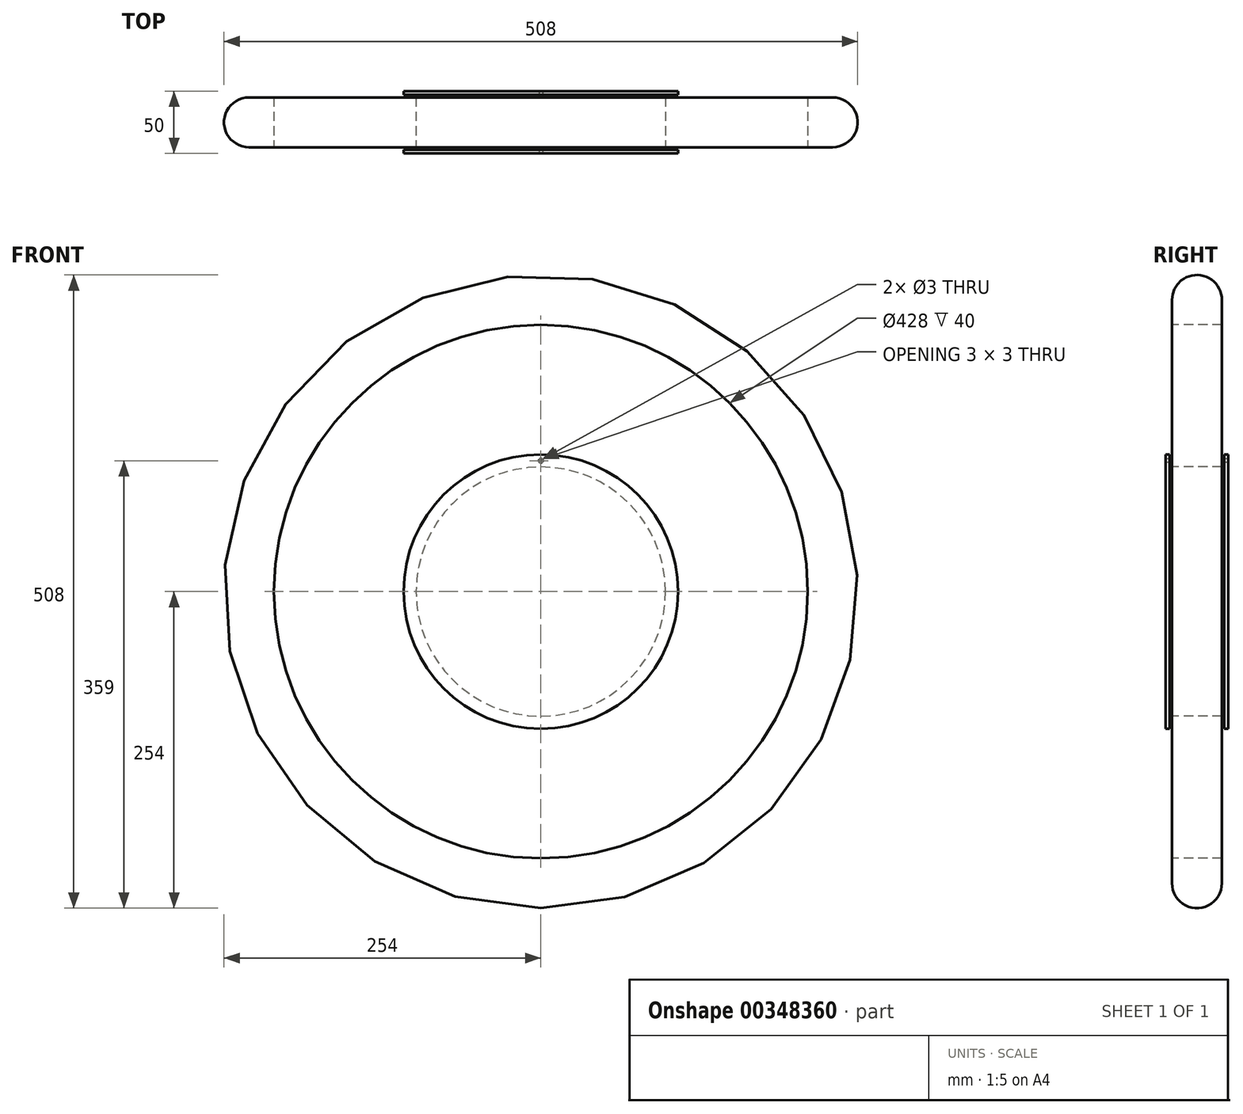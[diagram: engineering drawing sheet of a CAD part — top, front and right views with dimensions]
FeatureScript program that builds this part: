
annotation { "Feature Type Name" : "Feature", "Feature Type Description" : "" }
export const myFeature = defineFeature(function(context is Context, id is Id, definition is map)
    precondition{}
    {
        {
            var Q0;
            Q0=qCreatedBy(makeId("Top.planeOp"),FACE);
            var sketch = newSketch(context, id + "F0", { "sketchPlane" : qUnion([Q0])});
            skLineSegment(sketch, "E0", {"start": v(0, 0) * mm, "end": v(0, 101.57) * mm});
            skSolve(sketch);
        }
        {
            var Q0;
            Q0=qCreatedBy(makeId("Right.planeOp"),FACE);
            var sketch = newSketch(context, id + "F1", { "sketchPlane" : qUnion([Q0])});
            skLineSegment(sketch, "E1", {"start": v(0, 0) * mm, "end": v(0, 100) * mm, "construction": true});
            skLineSegment(sketch, "E2.bottom", {"start": v(25, 100) * mm, "end": v(-25, 100) * mm});
            skLineSegment(sketch, "E2.top", {"start": v(25, 0) * mm, "end": v(-25, 0) * mm});
            skLineSegment(sketch, "E2.left", {"start": v(25, 100) * mm, "end": v(25, 0) * mm});
            skLineSegment(sketch, "E2.right", {"start": v(-25, 100) * mm, "end": v(-25, 0) * mm});
            skPoint(sketch, "E2.middle", {"position": v(0, 50) * mm});
            skLineSegment(sketch, "E3", {"start": v(-25, 100) * mm, "end": v(-25, 110) * mm});
            skLineSegment(sketch, "E4", {"start": v(-25, 110) * mm, "end": v(-22, 110) * mm});
            skLineSegment(sketch, "E5", {"start": v(-22, 110) * mm, "end": v(-22, 100) * mm});
            skLineSegment(sketch, "E6.MirrorCS", {"start": v(25, 100) * mm, "end": v(25, 110) * mm});
            skLineSegment(sketch, "E7.MirrorCS", {"start": v(22, 110) * mm, "end": v(22, 100) * mm});
            skLineSegment(sketch, "E8.MirrorCS", {"start": v(25, 110) * mm, "end": v(22, 110) * mm});
            skSolve(sketch);
        }
        {
            var Q0;
            Q0 = qSketchRegion(id + "F1", true);
            var Q1;
            Q1=sQuery(id+"F0.wireOp",EDGE,"E0");
            revolve(context, id + "F2", {"entities" : qUnion([Q0]), "axis" : qUnion([Q1]), "revolveType" : RevolveType.FULL});
        }
        {
            var Q0;
            Q0=qCreatedBy(makeId("Right.planeOp"),FACE);
            var sketch = newSketch(context, id + "F3", { "sketchPlane" : qUnion([Q0])});
            skLineSegment(sketch, "E9", {"start": v(0, 0) * mm, "end": v(0, 254) * mm, "construction": true});
            skLineSegment(sketch, "E10.bottom", {"start": v(20, 234) * mm, "end": v(-20, 234) * mm, "construction": true});
            skLineSegment(sketch, "E10.top", {"start": v(20, 214) * mm, "end": v(-20, 214) * mm});
            skLineSegment(sketch, "E10.left", {"start": v(20, 234) * mm, "end": v(20, 214) * mm});
            skLineSegment(sketch, "E10.right", {"start": v(-20, 234) * mm, "end": v(-20, 214) * mm});
            skPoint(sketch, "E10.middle", {"position": v(0, 224) * mm});
            skArc(sketch, "E11", {"start": v(20, 234) * mm, "mid": v(0, 254) * mm, "end": v(-20, 234) * mm});
            skSolve(sketch);
        }
        {
            var Q0;
            Q0=makeQuery(id+"F3.imprint","IMPRINT",FACE,{"disambiguationData":[TD([[makeQuery(id+"F3.imprint","IMPRINT",EDGE,{"derivedFrom":sQuery(id+"F3.wireOp",EDGE,"E10.top")}),-1.0]])]});
            var Q1;
            Q1=sQuery(id+"F0.wireOp",EDGE,"E0");
            revolve(context, id + "F4", {"entities" : qUnion([Q0]), "axis" : qUnion([Q1]), "revolveType" : RevolveType.FULL});
        }
        {
            var Q0;
            Q0=makeQuery(id+"F2.opRevolve","SWEPT_FACE",FACE,{"disambiguationData":[OSD([sQuery(id+"F1.wireOp",EDGE,"E2.right"),sQuery(id+"F1.wireOp",EDGE,"E3")])]});
            var sketch = newSketch(context, id + "F5", { "sketchPlane" : qUnion([Q0])});
            skCircle(sketch, "E12", {"center": v(0, 105) * mm, "radius": 1.5 * mm});
            skSolve(sketch);
        }
        {
            var Q0;
            Q0 = qSketchRegion(id + "F5", true);
            extrude(context, id + "F6", {"entities" : qUnion([Q0]), "operationType" : NewBodyOperationType.REMOVE, "endBound" : BoundingType.THROUGH_ALL, "oppositeDirection" : true, "depth" : 25 * mm});
        }
    });
